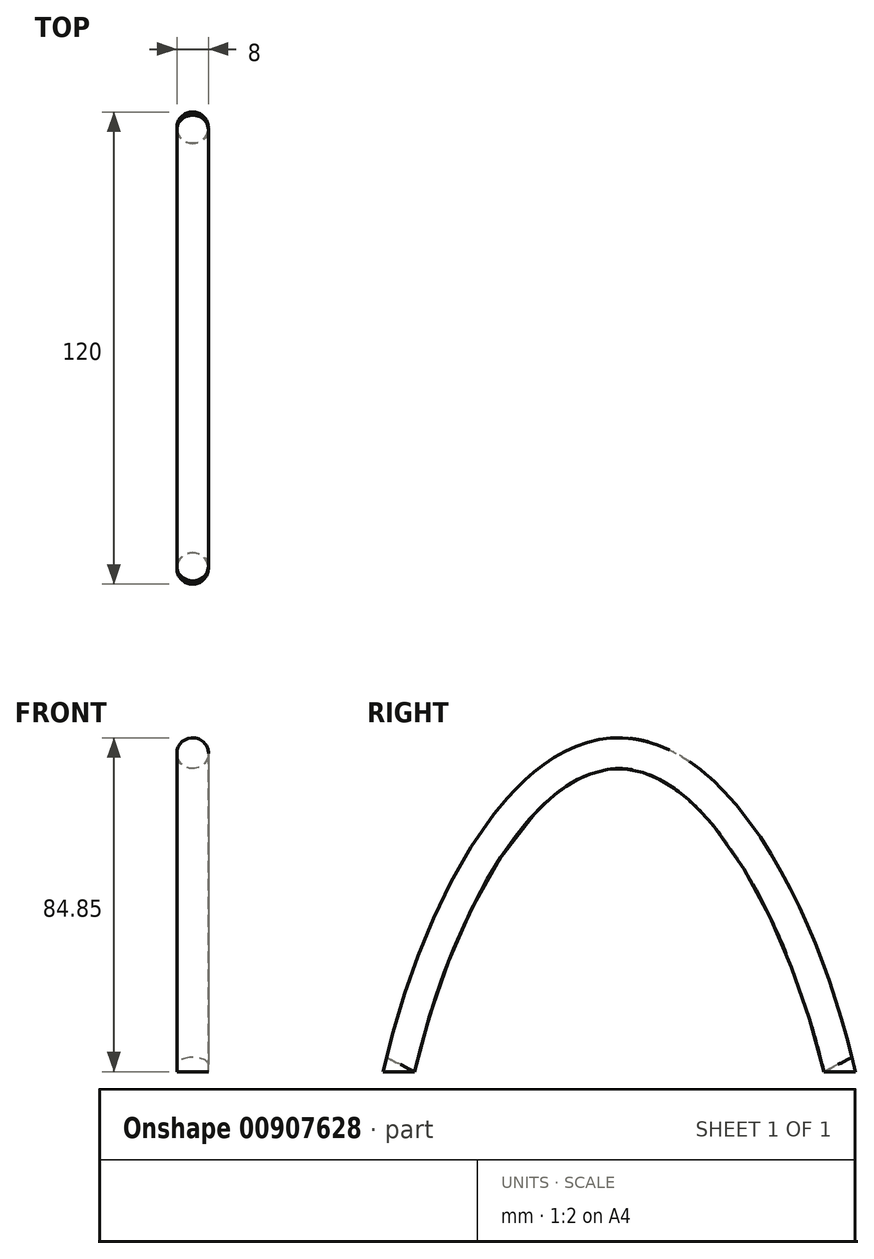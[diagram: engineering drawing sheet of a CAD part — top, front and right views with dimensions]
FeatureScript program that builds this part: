
annotation { "Feature Type Name" : "Feature", "Feature Type Description" : "" }
export const myFeature = defineFeature(function(context is Context, id is Id, definition is map)
    precondition{}
    {
        {
            var Q0;
            Q0=qCreatedBy(makeId("Right.planeOp"),FACE);
            var sketch = newSketch(context, id + "F0", { "sketchPlane" : qUnion([Q0])});
            skFitSpline(sketch, "E0", {"points": [v(-60, 0) * mm, v(0, 85) * mm, v(60, 0) * mm], "startDerivative": vector(60, 268.17) * mm, "endDerivative": vector(60, -273.4) * mm});
            skSolve(sketch);
        }
        {
            var Q0;
            Q0=qCreatedBy(makeId("Right.planeOp"),FACE);
            var sketch = newSketch(context, id + "F1", { "sketchPlane" : qUnion([Q0])});
            skFitSpline(sketch, "E1", {"points": [v(-52, 0) * mm, v(0, 77) * mm, v(52, 0) * mm], "startDerivative": vector(60, 253.2) * mm, "endDerivative": vector(60, -250.12) * mm});
            skLineSegment(sketch, "E2", {"start": v(-60, 0) * mm, "end": v(-52, 0) * mm});
            skLineSegment(sketch, "E3", {"start": v(52, 0) * mm, "end": v(60, 0) * mm});
            skSolve(sketch);
        }
        {
            var Q0;
            Q0=qCreatedBy(makeId("Top.planeOp"),FACE);
            var sketch = newSketch(context, id + "F2", { "sketchPlane" : qUnion([Q0])});
            skCircle(sketch, "E4", {"center": v(0, 56) * mm, "radius": 4 * mm});
            skCircle(sketch, "E5", {"center": v(0, -56) * mm, "radius": 4 * mm});
            skSolve(sketch);
        }
        {
            var Q0;
            Q0=makeQuery(id+"F2.imprint","IMPRINT",FACE,{"disambiguationData":[TD([[makeQuery(id+"F2.imprint","IMPRINT",EDGE,{"derivedFrom":sQuery(id+"F2.wireOp",EDGE,"E4")}),1.0]])]});
            var Q1;
            Q1=makeQuery(id+"F2.imprint","IMPRINT",FACE,{"disambiguationData":[TD([[makeQuery(id+"F2.imprint","IMPRINT",EDGE,{"derivedFrom":sQuery(id+"F2.wireOp",EDGE,"E5")}),1.0]])]});
            var Q2;
            Q2=sQuery(id+"F1.wireOp",EDGE,"E1");
            sweep(context, id + "F3", {"profiles" : qUnion([Q0, Q1]), "path" : qUnion([Q2])});
        }
    });
